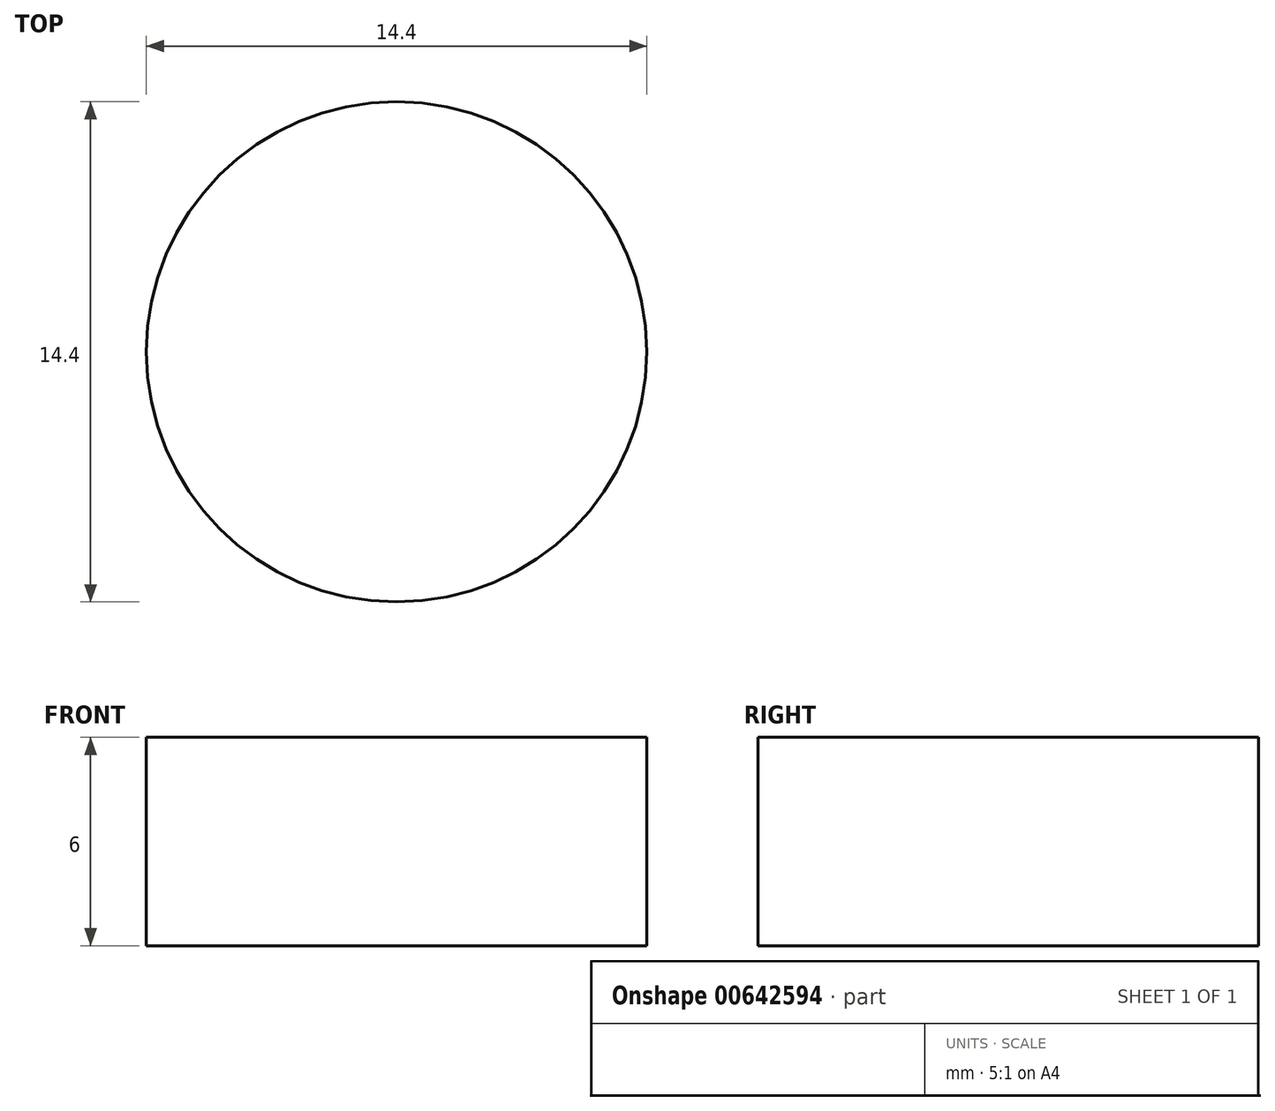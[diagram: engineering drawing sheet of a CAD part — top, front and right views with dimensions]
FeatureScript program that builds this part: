
annotation { "Feature Type Name" : "Feature", "Feature Type Description" : "" }
export const myFeature = defineFeature(function(context is Context, id is Id, definition is map)
    precondition{}
    {
        {
            var Q0;
            Q0=qCreatedBy(makeId("Top.planeOp"),FACE);
            var sketch = newSketch(context, id + "F0", { "sketchPlane" : qUnion([Q0])});
            skCircle(sketch, "E0", {"center": v(0, 0) * mm, "radius": 7.2 * mm});
            skSolve(sketch);
        }
        {
            var Q0;
            Q0 = qSketchRegion(id + "F0", true);
            extrude(context, id + "F1", {"entities" : qUnion([Q0]), "depth" : 6 * mm, "offsetDistance" : 25 * mm});
        }
    });
